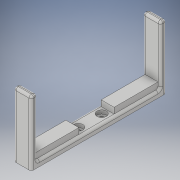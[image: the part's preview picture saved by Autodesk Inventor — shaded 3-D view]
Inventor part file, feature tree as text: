
AUTODESK INVENTOR PART (.ipt)
format: ipt  version: 2019.4 (Build 234330000, 330)  size: 200,704 bytes
history: native  units: mm
features: extrude x5, sketch x5, fillet x3
ambient origin geometry x8: Origin, YZ Plane, XZ Plane, XY Plane, X Axis, Y Axis, Z Axis, Center Point
bodies: Solid1 (feature_tree)
feature tree (13):
  extrude  "Extrusion1"  Depth=15.0mm
  extrude  "Extrusion2"  Depth=10.0mm
  extrude  "Extrusion3"  Depth=10.0mm
  extrude  "Extrusion4"  Depth=5.0mm TaperAngle=0.0deg
  fillet  "Fillet1"  Radius=8.0mm
  fillet  "Fillet2"  Radius=8.0mm
  fillet  "Fillet3"  Radius=3.0mm
  extrude  "Extrusion5"  Depth=5.0mm
  sketch  "Sketch1"  dims[d0=115.0mm d1=15.0mm]
  sketch  "Sketch2"  dims[d2=5.0mm d3=0.0mm d4=10.0mm]
  sketch  "Sketch3"  dims[d5=10.0mm d6=3.5mm]
  sketch  "Sketch4"  dims[d7=3.5mm d8=5.0mm d9=0.0mm d10=8.0mm d11=8.0mm d12=3.0mm d13=0.0mm]
  sketch  "Sketch5"  dims[d14=15.0mm d15=5.0mm d16=15.0mm d17=5.0mm d18=50.0mm d19=0.0mm d20=2.0mm d21=2.0mm d22=2.0mm d23=15.0mm d24=15.0mm d25=11.0mm d26=37.5mm d27=11.0mm d28=180.0deg d29=37.5mm d30=5.0mm d31=0.0mm]
